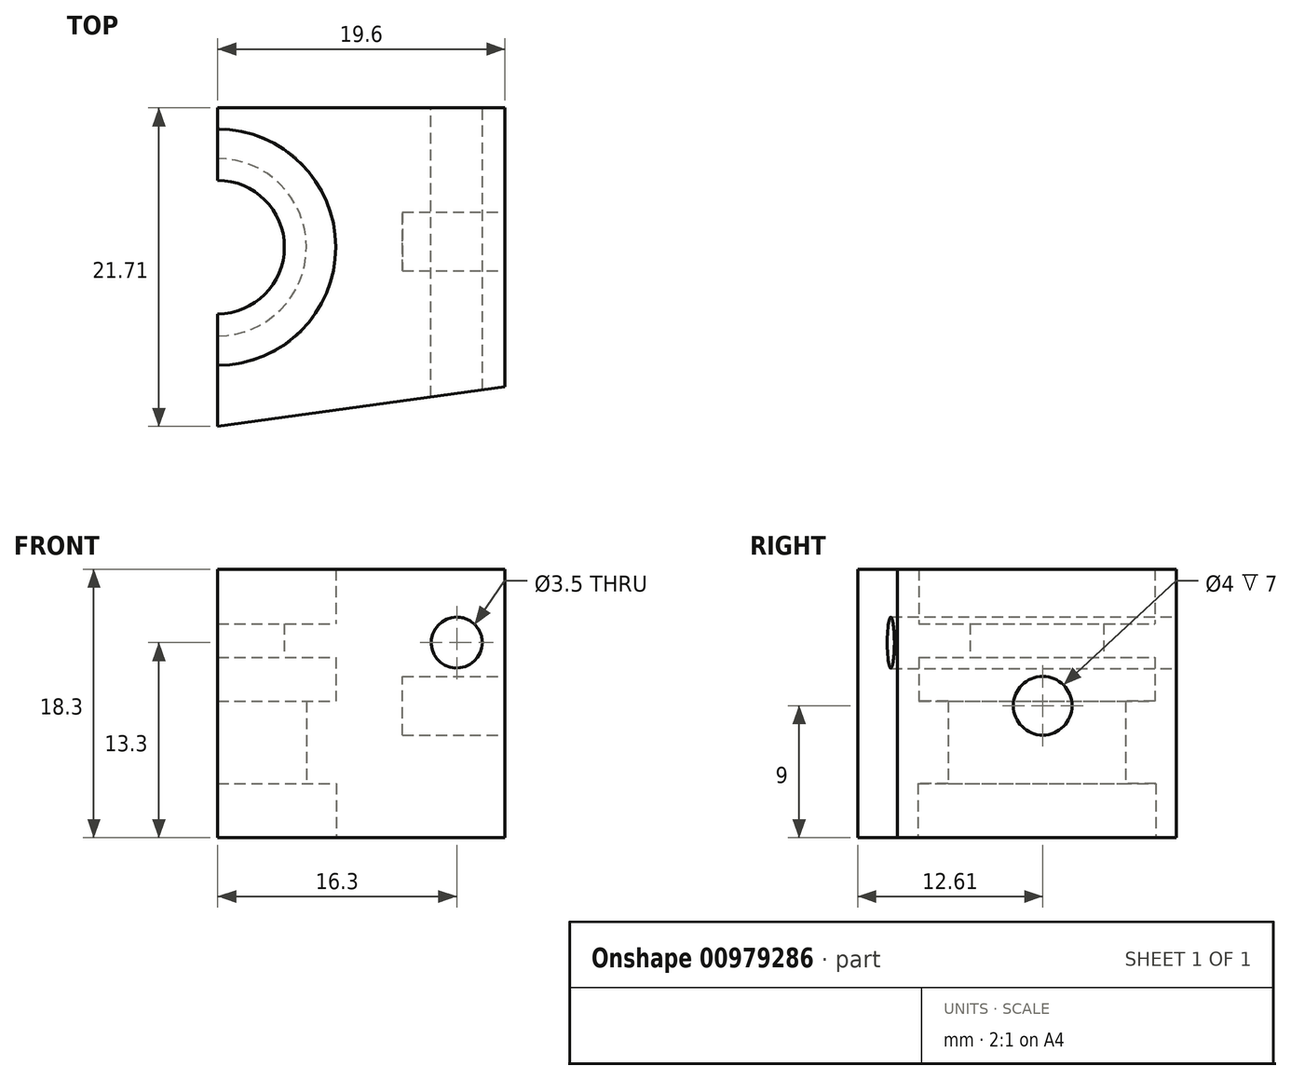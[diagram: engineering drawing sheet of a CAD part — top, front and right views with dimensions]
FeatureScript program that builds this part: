
annotation { "Feature Type Name" : "Feature", "Feature Type Description" : "" }
export const myFeature = defineFeature(function(context is Context, id is Id, definition is map)
    precondition{}
    {
        {
            var Q0;
            Q0=qCreatedBy(makeId("Top.planeOp"),FACE);
            var sketch = newSketch(context, id + "F0", { "sketchPlane" : qUnion([Q0])});
            skLineSegment(sketch, "E0", {"start": v(0, 12.21) * mm, "end": v(19.6, 9.5) * mm});
            skLineSegment(sketch, "E1", {"start": v(19.6, 9.5) * mm, "end": v(19.6, 0) * mm});
            skLineSegment(sketch, "E2", {"start": v(0, 12.21) * mm, "end": v(0, 0) * mm, "construction": true});
            skArc(sketch, "E3", {"start": v(8.1, 0) * mm, "mid": v(5.73, 5.73) * mm, "end": v(0, 8.1) * mm});
            skLineSegment(sketch, "E4", {"start": v(0, 12.21) * mm, "end": v(0, 8.1) * mm});
            skLineSegment(sketch, "E5.MirrorCS", {"start": v(0, -12.21) * mm, "end": v(0, -8.1) * mm});
            skLineSegment(sketch, "E6.MirrorCS", {"start": v(0, -12.21) * mm, "end": v(0, 0) * mm, "construction": true});
            skLineSegment(sketch, "E7.MirrorCS", {"start": v(0, -12.21) * mm, "end": v(19.6, -9.5) * mm});
            skLineSegment(sketch, "E8.MirrorCS", {"start": v(19.6, -9.5) * mm, "end": v(19.6, 0) * mm});
            skArc(sketch, "E9.MirrorCS", {"start": v(8.1, 0) * mm, "mid": v(5.73, -5.73) * mm, "end": v(0, -8.1) * mm});
            skSolve(sketch);
        }
        {
            var Q0;
            Q0=makeQuery(id+"F0.imprint","IMPRINT",FACE,{"disambiguationData":[TD([[makeQuery(id+"F0.imprint","IMPRINT",EDGE,{"derivedFrom":sQuery(id+"F0.wireOp",EDGE,"E0")}),-1.0]])]});
            extrude(context, id + "F1", {"entities" : qUnion([Q0]), "depth" : 3.7 * mm, "offsetDistance" : 25 * mm});
        }
        {
            var Q0;
            Q0=makeQuery(id+"F1.opExtrude","CAP_FACE",FACE,{"disambiguationData":[OSD([sQuery(id+"F0.wireOp",EDGE,"E0"),sQuery(id+"F0.wireOp",EDGE,"E1"),sQuery(id+"F0.wireOp",EDGE,"E3"),sQuery(id+"F0.wireOp",EDGE,"E4"),sQuery(id+"F0.wireOp",EDGE,"E5.MirrorCS"),sQuery(id+"F0.wireOp",EDGE,"E7.MirrorCS"),sQuery(id+"F0.wireOp",EDGE,"E8.MirrorCS"),sQuery(id+"F0.wireOp",EDGE,"E9.MirrorCS")])],"isStart":false});
            var sketch = newSketch(context, id + "F2", { "sketchPlane" : qUnion([Q0])});
            skArc(sketch, "E10", {"start": v(0, -6.05) * mm, "mid": v(6.05, 0) * mm, "end": v(0, 6.05) * mm});
            skLineSegment(sketch, "E11", {"start": v(0, 8.1) * mm, "end": v(0, 6.05) * mm});
            skLineSegment(sketch, "E12.trimOffspring", {"start": v(0, -6.05) * mm, "end": v(0, -8.1) * mm});
            skLineSegment(sketch, "E13", {"start": v(0, -8.1) * mm, "end": v(0, -12.21) * mm});
            skLineSegment(sketch, "E14", {"start": v(0, -12.2) * mm, "end": v(19.6, -9.5) * mm});
            skLineSegment(sketch, "E15", {"start": v(19.6, -9.5) * mm, "end": v(19.6, 9.5) * mm});
            skLineSegment(sketch, "E16", {"start": v(19.6, 9.5) * mm, "end": v(0, 12.2) * mm});
            skLineSegment(sketch, "E17", {"start": v(0, 12.21) * mm, "end": v(0, 8.1) * mm});
            skSolve(sketch);
        }
        {
            var Q0;
            Q0=qSketchRegion(id+"F2",true);
            extrude(context, id + "F3", {"entities" : qUnion([Q0]), "operationType" : NewBodyOperationType.ADD, "depth" : 5.6 * mm, "offsetDistance" : 25 * mm});
        }
        {
            var Q0;
            Q0=makeQuery(id+"F3.opExtrude","CAP_FACE",FACE,{"disambiguationData":[OSD([sQuery(id+"F2.wireOp",EDGE,"E10"),sQuery(id+"F2.wireOp",EDGE,"E11"),sQuery(id+"F2.wireOp",EDGE,"E12.trimOffspring"),sQuery(id+"F2.wireOp",EDGE,"E13"),sQuery(id+"F2.wireOp",EDGE,"E14"),sQuery(id+"F2.wireOp",EDGE,"E15"),sQuery(id+"F2.wireOp",EDGE,"E16"),sQuery(id+"F2.wireOp",EDGE,"E17")])],"isStart":false});
            var sketch = newSketch(context, id + "F4", { "sketchPlane" : qUnion([Q0])});
            skArc(sketch, "E18", {"start": v(0, -8.05) * mm, "mid": v(8.05, 0) * mm, "end": v(0, 8.05) * mm});
            skLineSegment(sketch, "E19", {"start": v(0, 8.05) * mm, "end": v(0, 12.21) * mm});
            skLineSegment(sketch, "E20", {"start": v(0, 12.2) * mm, "end": v(19.6, 9.5) * mm});
            skLineSegment(sketch, "E21", {"start": v(19.6, 9.5) * mm, "end": v(19.6, -9.5) * mm});
            skLineSegment(sketch, "E22", {"start": v(19.6, -9.5) * mm, "end": v(0, -12.2) * mm});
            skLineSegment(sketch, "E23", {"start": v(0, -12.21) * mm, "end": v(0, -8.05) * mm});
            skSolve(sketch);
        }
        {
            var Q0;
            Q0=qSketchRegion(id+"F4",true);
            extrude(context, id + "F5", {"entities" : qUnion([Q0]), "operationType" : NewBodyOperationType.ADD, "depth" : 3 * mm, "offsetDistance" : 25 * mm});
        }
        {
            var Q0;
            Q0=makeQuery(id+"F5.opExtrude","CAP_FACE",FACE,{"disambiguationData":[OSD([sQuery(id+"F4.wireOp",EDGE,"E18"),sQuery(id+"F4.wireOp",EDGE,"E19"),sQuery(id+"F4.wireOp",EDGE,"E20"),sQuery(id+"F4.wireOp",EDGE,"E21"),sQuery(id+"F4.wireOp",EDGE,"E22"),sQuery(id+"F4.wireOp",EDGE,"E23")])],"isStart":false});
            var sketch = newSketch(context, id + "F6", { "sketchPlane" : qUnion([Q0])});
            skArc(sketch, "E24", {"start": v(0, -4.55) * mm, "mid": v(4.55, 0) * mm, "end": v(0, 4.55) * mm});
            skLineSegment(sketch, "E25", {"start": v(0, 4.55) * mm, "end": v(0, 12.21) * mm});
            skLineSegment(sketch, "E26", {"start": v(0, 12.2) * mm, "end": v(19.6, 9.5) * mm});
            skLineSegment(sketch, "E27", {"start": v(19.6, 9.5) * mm, "end": v(19.6, -9.5) * mm});
            skLineSegment(sketch, "E28", {"start": v(19.6, -9.5) * mm, "end": v(0, -12.2) * mm});
            skLineSegment(sketch, "E29", {"start": v(0, -12.21) * mm, "end": v(0, -4.55) * mm});
            skSolve(sketch);
        }
        {
            var Q0;
            Q0=qSketchRegion(id+"F6",true);
            extrude(context, id + "F7", {"entities" : qUnion([Q0]), "operationType" : NewBodyOperationType.ADD, "depth" : 2.3 * mm, "offsetDistance" : 25 * mm});
        }
        {
            var Q0;
            Q0=makeQuery(id+"F7.opExtrude","CAP_FACE",FACE,{"disambiguationData":[OSD([sQuery(id+"F6.wireOp",EDGE,"E24"),sQuery(id+"F6.wireOp",EDGE,"E25"),sQuery(id+"F6.wireOp",EDGE,"E26"),sQuery(id+"F6.wireOp",EDGE,"E27"),sQuery(id+"F6.wireOp",EDGE,"E28"),sQuery(id+"F6.wireOp",EDGE,"E29")])],"isStart":false});
            var sketch = newSketch(context, id + "F8", { "sketchPlane" : qUnion([Q0])});
            skArc(sketch, "E30", {"start": v(0, -8.05) * mm, "mid": v(8.05, 0) * mm, "end": v(0, 8.05) * mm});
            skLineSegment(sketch, "E31", {"start": v(0, 8.05) * mm, "end": v(0, 12.21) * mm});
            skLineSegment(sketch, "E32", {"start": v(0, 12.2) * mm, "end": v(19.6, 9.5) * mm});
            skLineSegment(sketch, "E33", {"start": v(19.6, 9.5) * mm, "end": v(19.6, -9.5) * mm});
            skLineSegment(sketch, "E34", {"start": v(19.6, -9.5) * mm, "end": v(0, -12.2) * mm});
            skLineSegment(sketch, "E35", {"start": v(0, -12.21) * mm, "end": v(0, -8.05) * mm});
            skSolve(sketch);
        }
        {
            var Q0;
            Q0=qSketchRegion(id+"F8",true);
            extrude(context, id + "F9", {"entities" : qUnion([Q0]), "operationType" : NewBodyOperationType.ADD, "depth" : 3.7 * mm, "offsetDistance" : 25 * mm});
        }
        {
            var Q0;
            Q0=makeQuery(id+"F1.opExtrude","CAP_FACE",FACE,{"disambiguationData":[OSD([sQuery(id+"F0.wireOp",EDGE,"E0"),sQuery(id+"F0.wireOp",EDGE,"E1"),sQuery(id+"F0.wireOp",EDGE,"E3"),sQuery(id+"F0.wireOp",EDGE,"E4"),sQuery(id+"F0.wireOp",EDGE,"E5.MirrorCS"),sQuery(id+"F0.wireOp",EDGE,"E7.MirrorCS"),sQuery(id+"F0.wireOp",EDGE,"E8.MirrorCS"),sQuery(id+"F0.wireOp",EDGE,"E9.MirrorCS")])],"isStart":true});
            var sketch = newSketch(context, id + "F10", { "sketchPlane" : qUnion([Q0])});
            skLineSegment(sketch, "E36", {"start": v(19.6, -9.5) * mm, "end": v(0, -9.5) * mm});
            skLineSegment(sketch, "E37", {"start": v(0, -9.5) * mm, "end": v(0, -12.21) * mm});
            skLineSegment(sketch, "E38", {"start": v(0, -12.2) * mm, "end": v(19.6, -9.5) * mm});
            skSolve(sketch);
        }
        {
            var Q0;
            Q0=qSketchRegion(id+"F10",true);
            extrude(context, id + "F11", {"entities" : qUnion([Q0]), "operationType" : NewBodyOperationType.REMOVE, "oppositeDirection" : true, "depth" : 25 * mm, "offsetDistance" : 25 * mm, "hasSecondDirection" : true, "secondDirectionOppositeDirection" : false, "secondDirectionDepth" : 25 * mm});
        }
        {
            var Q0;
            Q0=makeQuery(id+"F9.boolean.opBoolean","MERGE",FACE,{"derivedFrom":[makeQuery(id+"F7.boolean.opBoolean","MERGE",FACE,{"derivedFrom":[makeQuery(id+"F5.boolean.opBoolean","MERGE",FACE,{"derivedFrom":[makeQuery(id+"F3.boolean.opBoolean","MERGE",FACE,{"derivedFrom":[makeQuery(id+"F1.opExtrude","SWEPT_FACE",FACE,{"disambiguationData":[OSD([sQuery(id+"F0.wireOp",EDGE,"E1"),sQuery(id+"F0.wireOp",EDGE,"E8.MirrorCS")])]}),makeQuery(id+"F3.opExtrude","SWEPT_FACE",FACE,{"disambiguationData":[OSD([sQuery(id+"F2.wireOp",EDGE,"E15")])]})]}),makeQuery(id+"F5.opExtrude","SWEPT_FACE",FACE,{"disambiguationData":[OSD([sQuery(id+"F4.wireOp",EDGE,"E21")])]})]}),makeQuery(id+"F7.opExtrude","SWEPT_FACE",FACE,{"disambiguationData":[OSD([sQuery(id+"F6.wireOp",EDGE,"E27")])]})]}),makeQuery(id+"F9.opExtrude","SWEPT_FACE",FACE,{"disambiguationData":[OSD([sQuery(id+"F8.wireOp",EDGE,"E33")])]})]});
            var sketch = newSketch(context, id + "F12", { "sketchPlane" : qUnion([Q0])});
            skLineSegment(sketch, "E39", {"start": v(9.5, 9) * mm, "end": v(0.4, 9) * mm, "construction": true});
            skLineSegment(sketch, "E40", {"start": v(0.4, 9) * mm, "end": v(0.4, 18.3) * mm, "construction": true});
            skCircle(sketch, "E41", {"center": v(0.4, 9) * mm, "radius": 2 * mm});
            skSolve(sketch);
        }
        {
            var Q0;
            Q0=qSketchRegion(id+"F12",true);
            extrude(context, id + "F13", {"entities" : qUnion([Q0]), "operationType" : NewBodyOperationType.REMOVE, "oppositeDirection" : true, "depth" : 7 * mm, "offsetDistance" : 25 * mm});
        }
        {
            var Q0;
            Q0=makeQuery(id+"F11.boolean.opBoolean","COPY",FACE,{"derivedFrom":makeQuery(id+"F11.opExtrude","SWEPT_FACE",FACE,{"disambiguationData":[OSD([sQuery(id+"F10.wireOp",EDGE,"E36")])]})});
            var sketch = newSketch(context, id + "F14", { "sketchPlane" : qUnion([Q0])});
            skLineSegment(sketch, "E42", {"start": v(-19.6, 13.3) * mm, "end": v(-16.3, 13.3) * mm, "construction": true});
            skLineSegment(sketch, "E43", {"start": v(-16.3, 13.3) * mm, "end": v(-16.3, 18.3) * mm, "construction": true});
            skCircle(sketch, "E44", {"center": v(-16.3, 13.3) * mm, "radius": 1.75 * mm});
            skSolve(sketch);
        }
        {
            var Q0;
            Q0=qSketchRegion(id+"F14",true);
            extrude(context, id + "F15", {"entities" : qUnion([Q0]), "operationType" : NewBodyOperationType.REMOVE, "oppositeDirection" : true, "depth" : 25 * mm, "offsetDistance" : 25 * mm});
        }
    });
